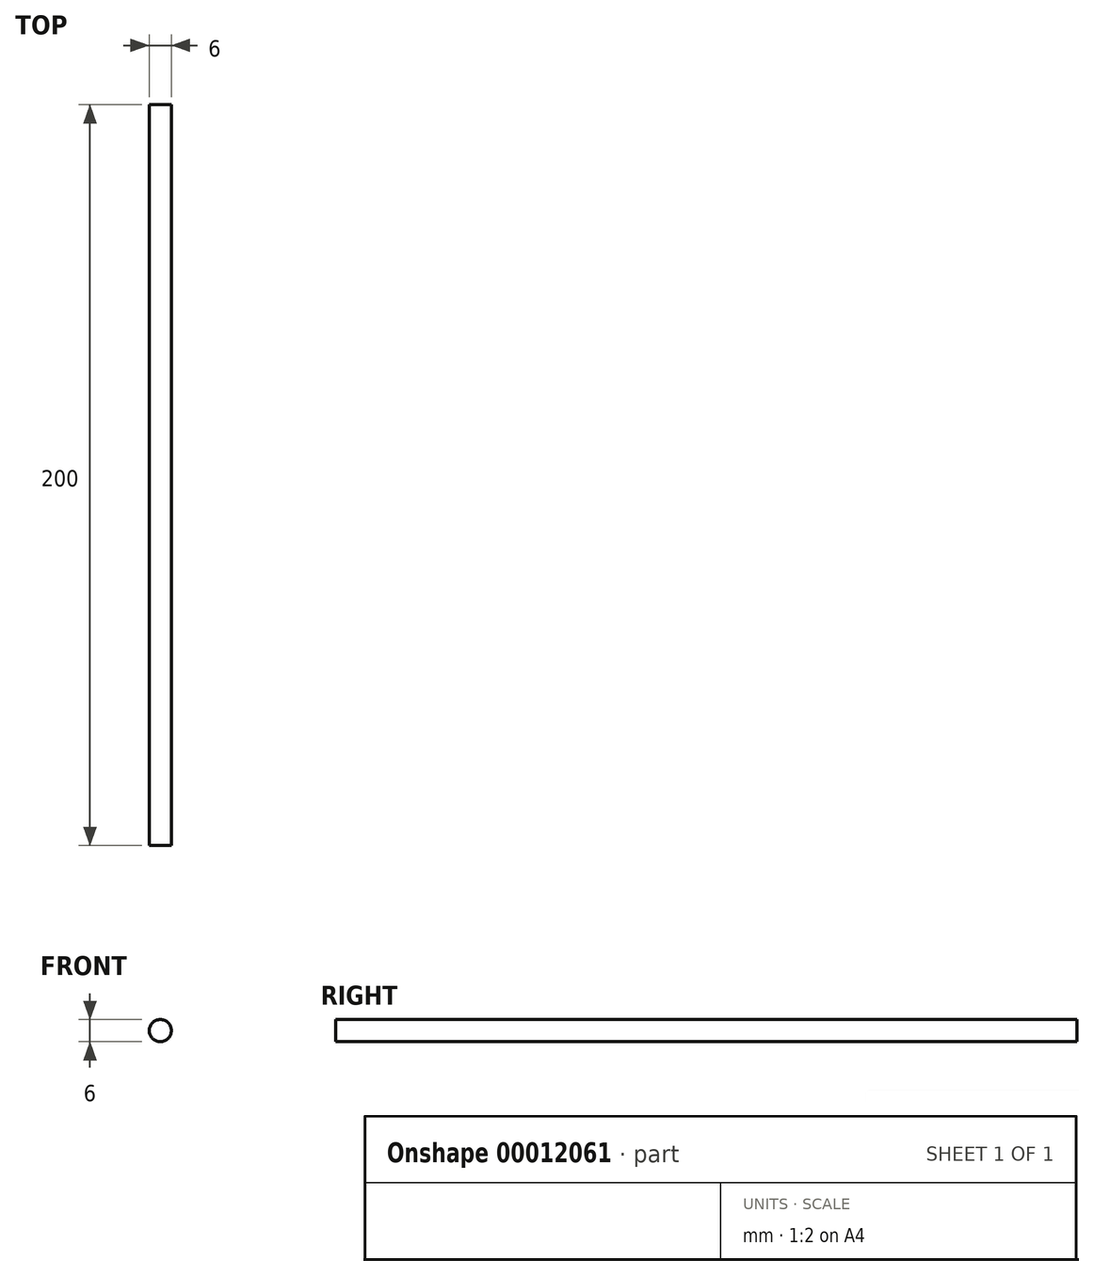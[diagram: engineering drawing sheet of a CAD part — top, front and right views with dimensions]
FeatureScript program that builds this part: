
annotation { "Feature Type Name" : "Feature", "Feature Type Description" : "" }
export const myFeature = defineFeature(function(context is Context, id is Id, definition is map)
    precondition{}
    {
        {
            var Q0;
            Q0=qCreatedBy(makeId("Front.planeOp"),FACE);
            var sketch = newSketch(context, id + "F0", { "sketchPlane" : qUnion([Q0])});
            skCircle(sketch, "E0", {"center": v(-119.49, 39.55) * mm, "radius": 3 * mm});
            skSolve(sketch);
        }
        {
            var Q0;
            Q0 = qSketchRegion(id + "F0", true);
            extrude(context, id + "F1", {"entities" : qUnion([Q0]), "depth" : 200 * mm});
        }
    });
